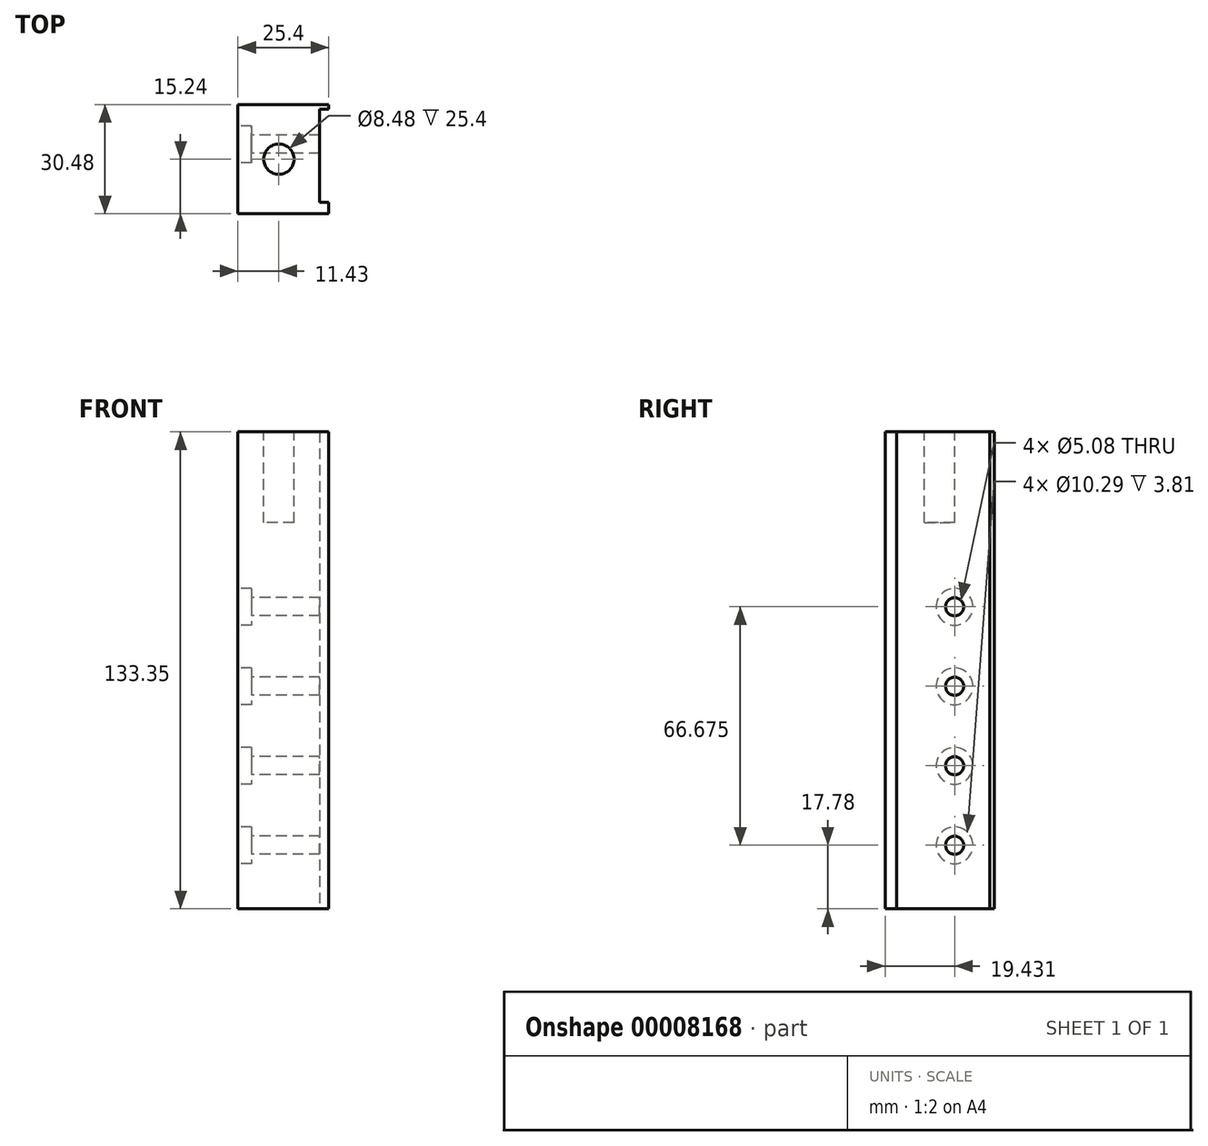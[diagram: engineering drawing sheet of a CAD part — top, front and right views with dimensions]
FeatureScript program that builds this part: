
annotation { "Feature Type Name" : "Feature", "Feature Type Description" : "" }
export const myFeature = defineFeature(function(context is Context, id is Id, definition is map)
    precondition{}
    {
        {
            var Q0;
            Q0=qCreatedBy(makeId("Top.planeOp"),FACE);
            var sketch = newSketch(context, id + "F0", { "sketchPlane" : qUnion([Q0])});
            skLineSegment(sketch, "E0.rect.bottom", {"start": v(-12.7, -15.24) * mm, "end": v(12.7, -15.24) * mm});
            skLineSegment(sketch, "E0.rect.top", {"start": v(-12.7, 15.24) * mm, "end": v(12.7, 15.24) * mm});
            skLineSegment(sketch, "E0.rect.left", {"start": v(-12.7, -15.24) * mm, "end": v(-12.7, 15.24) * mm});
            skLineSegment(sketch, "E0.rect.right", {"start": v(12.7, -15.24) * mm, "end": v(12.7, 15.24) * mm});
            skPoint(sketch, "E0.rect.middle", {"position": v(0, 0) * mm});
            skSolve(sketch);
        }
        {
            var Q0;
            Q0=qSketchRegion(id+"F0",true);
            extrude(context, id + "F1", {"entities" : qUnion([Q0]), "oppositeDirection" : true, "depth" : 133.35 * mm});
        }
        {
            var Q0;
            Q0=makeQuery(id+"F1.opExtrude","SWEPT_FACE",FACE,{"disambiguationData":[OSD([sQuery(id+"F0.wireOp",EDGE,"E0.rect.left")])]});
            var sketch = newSketch(context, id + "F2", { "sketchPlane" : qUnion([Q0])});
            skCircle(sketch, "E1", {"center": v(-4.2, -71.12) * mm, "radius": 2.54 * mm});
            skCircle(sketch, "E2", {"center": v(-4.2, -115.57) * mm, "radius": 2.54 * mm});
            skCircle(sketch, "E3", {"center": v(-4.2, -48.9) * mm, "radius": 2.54 * mm});
            skCircle(sketch, "E4", {"center": v(-4.2, -93.35) * mm, "radius": 2.54 * mm});
            skSolve(sketch);
        }
        {
            var Q0;
            Q0=qSketchRegion(id+"F2",true);
            extrude(context, id + "F3", {"entities" : qUnion([Q0]), "operationType" : NewBodyOperationType.REMOVE, "endBound" : BoundingType.UP_TO_NEXT, "oppositeDirection" : true, "depth" : 25.4 * mm});
        }
        {
            var Q0;
            Q0=makeQuery(id+"F1.opExtrude","SWEPT_FACE",FACE,{"disambiguationData":[OSD([sQuery(id+"F0.wireOp",EDGE,"E0.rect.left")])]});
            var sketch = newSketch(context, id + "F4", { "sketchPlane" : qUnion([Q0])});
            skCircle(sketch, "E5", {"center": v(-4.2, -71.12) * mm, "radius": 5.14 * mm});
            skCircle(sketch, "E6", {"center": v(-4.2, -115.57) * mm, "radius": 5.14 * mm});
            skCircle(sketch, "E7", {"center": v(-4.2, -48.9) * mm, "radius": 5.14 * mm});
            skCircle(sketch, "E8", {"center": v(-4.2, -93.35) * mm, "radius": 5.14 * mm});
            skSolve(sketch);
        }
        {
            var Q0;
            Q0=qSketchRegion(id+"F4",true);
            extrude(context, id + "F5", {"entities" : qUnion([Q0]), "operationType" : NewBodyOperationType.REMOVE, "oppositeDirection" : true, "depth" : 3.8 * mm});
        }
        {
            var Q0;
            Q0=makeQuery(id+"F1.opExtrude","CAP_FACE",FACE,{"disambiguationData":[OSD([sQuery(id+"F0.wireOp",EDGE,"E0.rect.bottom"),sQuery(id+"F0.wireOp",EDGE,"E0.rect.top"),sQuery(id+"F0.wireOp",EDGE,"E0.rect.left"),sQuery(id+"F0.wireOp",EDGE,"E0.rect.right")])],"isStart":true});
            var sketch = newSketch(context, id + "F6", { "sketchPlane" : qUnion([Q0])});
            skCircle(sketch, "E9", {"center": v(-1.27, 0) * mm, "radius": 4.24 * mm});
            skSolve(sketch);
        }
        {
            var Q0;
            Q0 = qSketchRegion(id + "F6", true);
            extrude(context, id + "F7", {"entities" : qUnion([Q0]), "operationType" : NewBodyOperationType.REMOVE, "oppositeDirection" : true, "depth" : 25.4 * mm});
        }
        {
            var Q0;
            Q0=makeQuery(id+"F1.opExtrude","SWEPT_FACE",FACE,{"disambiguationData":[OSD([sQuery(id+"F0.wireOp",EDGE,"E0.rect.right")])]});
            var sketch = newSketch(context, id + "F8", { "sketchPlane" : qUnion([Q0])});
            skLineSegment(sketch, "E10.bottom", {"start": v(13.97, 0) * mm, "end": v(-12.07, 0) * mm});
            skLineSegment(sketch, "E10.top", {"start": v(13.97, -133.35) * mm, "end": v(-12.06, -133.35) * mm});
            skLineSegment(sketch, "E10.left", {"start": v(13.97, 0) * mm, "end": v(13.97, -133.35) * mm});
            skLineSegment(sketch, "E10.right", {"start": v(-12.07, 0) * mm, "end": v(-12.06, -133.35) * mm});
            skSolve(sketch);
        }
        {
            var Q0;
            Q0 = qSketchRegion(id + "F8", true);
            extrude(context, id + "F9", {"entities" : qUnion([Q0]), "operationType" : NewBodyOperationType.REMOVE, "oppositeDirection" : true, "depth" : 2.54 * mm});
        }
    });
